# Revit family: Basin-Console-DXV-Belshire-D190800000
name_source: partatom
category: Plumbing Fixtures
revit_build: Autodesk Revit 2016 (Build: 20150714_1515(x64)
units: mm (PartAtom-declared; Revit-internal decimal feet)

## family parameters
Always vertical = Yes
Cut with Voids When Loaded = No
OmniClass Number = 23.45.05.14.14
OmniClass Title = Sinks/Lavatories
Part Type = Normal
Room Calculation Point = No
Round Connector Dimension = Use Diameter
Shared = Yes
Work Plane-Based = No

## types (1)
- D190800000
    Assembly Code = D2010300
    Basin Shape = Rectangular
    CW Connection = Yes
    CWFU = 1.5
    Connection Size = 1/2"
    Countertop Finish = Marble-DXV-550-Carrara
    Description = DXV BELSHIRE™ CONSOLE
    HW Connection = Yes
    HWFU = 1.5
    Height = 36 1/2"
    Installation Type = Floor Mounted
    Length = 22 3/8"
    Manufacturer = DXV
    Model = D190800000
    Price = Prices may vary. Please consult Manufacturer Representative for most up-to-date price list.
    URL = https://www.dxv.com
    Vanity Leg Set Finish = Metal-DXV-427-Satin Brass
    Vent Connection = No
    WFU = 2
    Warranty Documentation Link = https://www.dxv.com
    Waste Connection = Yes
    Waste Connection Diameter = 1 1/4"
    Width = 30"

## geometry (parser evidence)
native form markers: Sweep x5
no freeform markers — native parametric forms only
